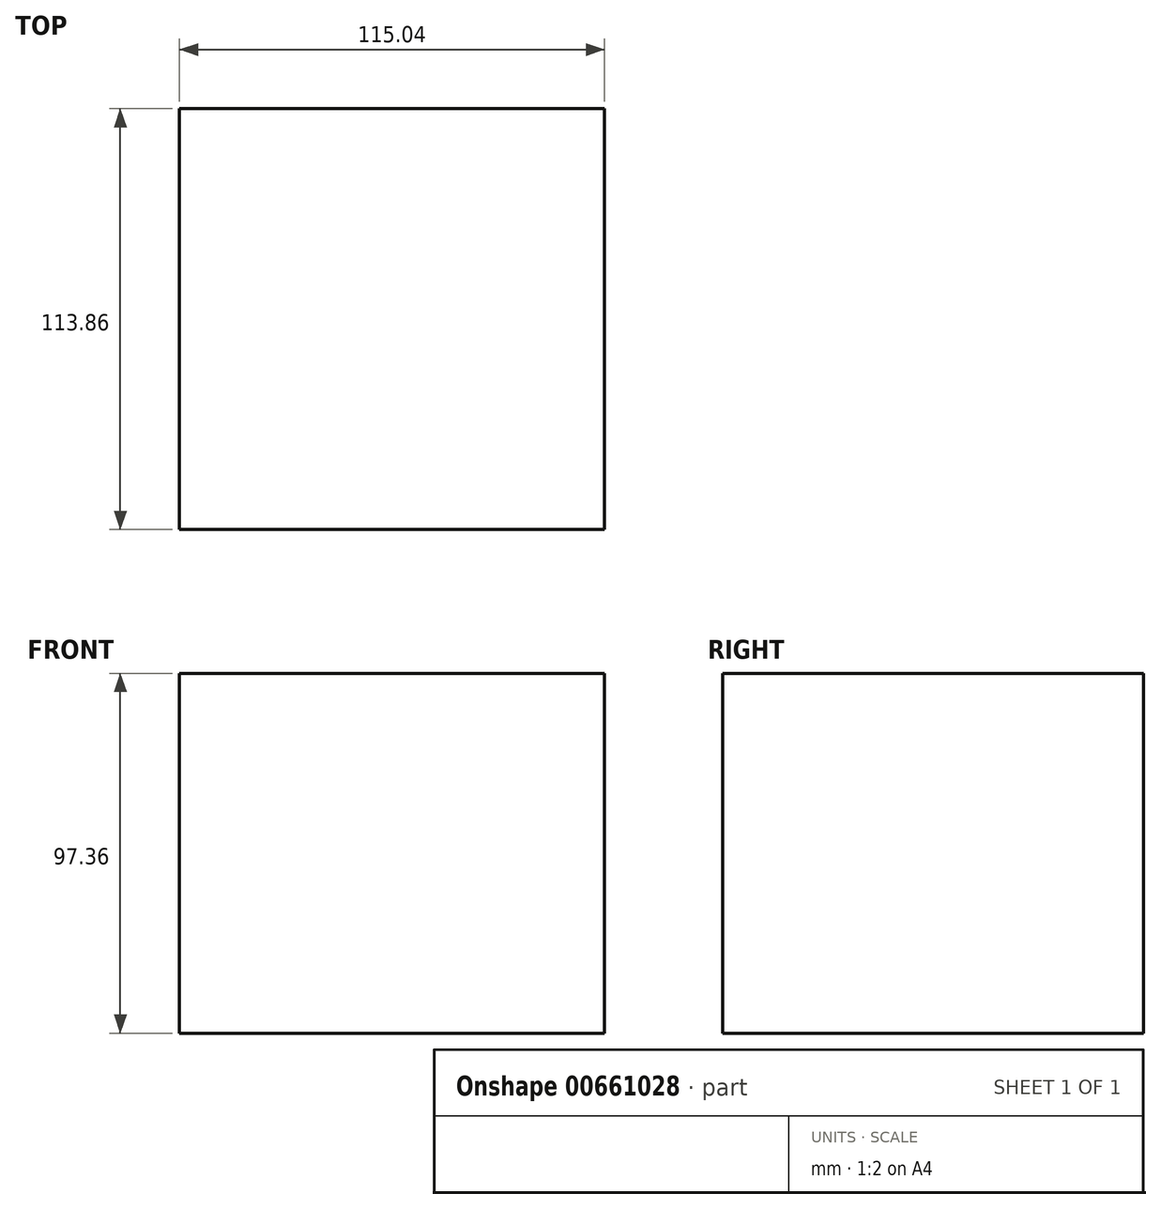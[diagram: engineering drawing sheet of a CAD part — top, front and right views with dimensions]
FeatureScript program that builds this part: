
annotation { "Feature Type Name" : "Feature", "Feature Type Description" : "" }
export const myFeature = defineFeature(function(context is Context, id is Id, definition is map)
    precondition{}
    {
        {
            var Q0;
            Q0=qCreatedBy(makeId("Front.planeOp"),FACE);
            var sketch = newSketch(context, id + "F0", { "sketchPlane" : qUnion([Q0])});
            skLineSegment(sketch, "E0.bottom", {"start": v(0, 23.67) * mm, "end": v(115.04, 23.67) * mm});
            skLineSegment(sketch, "E0.top", {"start": v(0, 121.03) * mm, "end": v(115.04, 121.03) * mm});
            skLineSegment(sketch, "E0.left", {"start": v(0, 23.67) * mm, "end": v(0, 121.03) * mm});
            skLineSegment(sketch, "E0.right", {"start": v(115.04, 23.67) * mm, "end": v(115.04, 121.03) * mm});
            skPoint(sketch, "E0.middle", {"position": v(57.52, 72.35) * mm});
            skSolve(sketch);
        }
        {
            var Q0;
            Q0 = qSketchRegion(id + "F0", true);
            extrude(context, id + "F1", {"entities" : qUnion([Q0]), "depth" : 113.86 * mm, "offsetDistance" : 25.4 * mm});
        }
    });
